# Revit family: Hager-GOLF-Flush_mounted-IP40-With_Cover-With_DIN-Hosted-CH-fr
name_source: partatom
category: Electrical Equipment
units: mm (PartAtom-declared; Revit-internal decimal feet)

## family parameters
Cut with Voids When Loaded = No
Host = Face
Maintain Annotation Orientation = Yes
Panel Configuration = Two Columns, Circuits Across
Part Type = Panelboard
Room Calculation Point = No
Round Connector Dimension = Use Diameter
Shared = No

## types (20) — shared parameters
BC_MODEL_ID = 1539117
BC_OBJECT_ID = 512264
BC_OBJECT_VERSION = #40
Code hager = ADD-EC000214_EU
EF000003 - Mounting method = Flush-mounted
EF000007 - Colour = White
EF000024 - UV resistant = No
EF000049 - Depth = 97 mm  [stored 0.318241 ft]
EF000116 - RAL-number = 9010
EF000118 - With mounting plate = No
EF000218 - Built-in depth = 72 mm  [stored 0.23622 ft]
EF001062 - EMC-version = No
EF001088 - Extension possible = Yes
EF001134 - DIN-rail = Yes
EF004462 - Type of closure = Other
EF005474 - Degree of protection (IP) = IP40
EF006306 - With lock = No
EF009212 - Cover model = Closed
EF015941 - Signal passing door = Yes
ETIM class code = EC000214
ETIM class name = Small distribution board
HG000001-Number of columns = 1
HG000002-With door or cover = Yes
HG000003-Range = GOLF
HG000005-Thickness = 2 mm  [stored 0.00656168 ft]
HG000006-Flush mounted = Yes
HG000009-Double swing door = No
HG000010-Asymmetric doors = No
HG000011-Empty rows from bottom = No
HG000012-Door swing angle = 90.00°
HG000013-Door on the left = No
HG000014-Door on the right = Yes
HG000015-Clearance visibility = Yes
HG000016-Door 3D visibility = Yes
HG000017-Distance between poles = 18 mm  [stored 0.0590551 ft]
HG000060-RAL-number = 9010
HG000099-Onfly Template ID = 507532
Manufacturer = Hager
Name = GOLF-Flush_mounted-IP40-With_Cover-With_DIN-CH
Name BIM&CO = Electricity
Name hager = ADD_Enclosures_EC000214
Uniformat = Low Tension Service & Dist.
Uniformat code = D501001
zero-valued in all types: Default Elevation, EF001131 - Inner depth, HG000007-Number of empty columns, HG000008-Number of empty rows

## per-type parameters (varying)
| type | BC_METADATA | BC_VARIANT_ID | EF000008 - Width | EF000040 - Height | EF000266 - Number of rows | EF000332 - Built-in height | EF000846 - Built-in width | EF002950 - Width in number of modular spacings | EF006244 - Transparent cover/door | EF015776 - Earthing terminal block | EF015777 - Neutral terminal block | HG000004-Manufacturer reference | HGEF000266-Number of rows | HGEF002950-Width in number of modular spacings |
| GOLF-Flush_mounted_W204_H225_D97_4_Modular_Spacing-VF104PS | {"ObjectGuid":"d3b36538-3273-4197-a562-01bf94599a27","ModelGuid":"35c68a91-80b1-4e81-b496-b66524f3143e","VariantGuid":"7900b5fb-65a8-428c-881f-07103e9f7ffe","Revision":"#25","VariantName":"GOLF-Flush_mounted_W204_H225_D97_4_Modular_Spacing-VF104PS"} | 1169077 | 204 mm | 225 mm  [stored 0.738189 ft] | 1 | 189 mm  [stored 0.620079 ft] | 170 mm  [stored 0.557743 ft] | 4 | No | No | No | VF104PS | 1 | 4 |
| GOLF-Flush_mounted_W204_H225_D97_4_Modular_Spacing-VF104TS | {"ObjectGuid":"d3b36538-3273-4197-a562-01bf94599a27","ModelGuid":"35c68a91-80b1-4e81-b496-b66524f3143e","VariantGuid":"d0b361cd-5e5f-4586-98f2-c8f494179b52","Revision":"#25","VariantName":"GOLF-Flush_mounted_W204_H225_D97_4_Modular_Spacing-VF104TS"} | 1169078 | 204 mm | 225 mm  [stored 0.738189 ft] | 1 | 189 mm  [stored 0.620079 ft] | 170 mm  [stored 0.557743 ft] | 4 | Yes | No | No | VF104TS | 1 | 4 |
| GOLF-Flush_mounted_W275_H225_D97_8_Modular_Spacing-VF108PS | {"ObjectGuid":"d3b36538-3273-4197-a562-01bf94599a27","ModelGuid":"35c68a91-80b1-4e81-b496-b66524f3143e","VariantGuid":"570270ab-bc6c-4446-b563-185213bbcdad","Revision":"#25","VariantName":"GOLF-Flush_mounted_W275_H225_D97_8_Modular_Spacing-VF108PS"} | 1169079 | 275 mm | 225 mm  [stored 0.738189 ft] | 1 | 189 mm  [stored 0.620079 ft] | 242 mm  [stored 0.793963 ft] | 8 | No | No | No | VF108PS | 1 | 8 |
| GOLF-Flush_mounted_W275_H225_D97_8_Modular_Spacing-VF108TS | {"ObjectGuid":"d3b36538-3273-4197-a562-01bf94599a27","ModelGuid":"35c68a91-80b1-4e81-b496-b66524f3143e","VariantGuid":"a5ca7ae0-c990-4f4f-958b-64a5adfce291","Revision":"#25","VariantName":"GOLF-Flush_mounted_W275_H225_D97_8_Modular_Spacing-VF108TS"} | 1169080 | 275 mm | 225 mm  [stored 0.738189 ft] | 1 | 189 mm  [stored 0.620079 ft] | 242 mm  [stored 0.793963 ft] | 8 | Yes | No | No | VF108TS | 1 | 8 |
| GOLF-Flush_mounted_W352_H293_D97_12_Modular_Spacing-VF112PS | {"ObjectGuid":"d3b36538-3273-4197-a562-01bf94599a27","ModelGuid":"35c68a91-80b1-4e81-b496-b66524f3143e","VariantGuid":"727fad79-9f42-4d6a-8770-c75fea08dc77","Revision":"#25","VariantName":"GOLF-Flush_mounted_W352_H293_D97_12_Modular_Spacing-VF112PS"} | 1169081 | 352 mm  [stored 1.15486 ft] | 293 mm | 1 | 257 mm  [stored 0.843176 ft] | 318 mm  [stored 1.04331 ft] | 12 | No | Yes | Yes | VF112PS | 1 | 12 |
| GOLF-Flush_mounted_W352_H293_D97_12_Modular_Spacing-VF112TS | {"ObjectGuid":"d3b36538-3273-4197-a562-01bf94599a27","ModelGuid":"35c68a91-80b1-4e81-b496-b66524f3143e","VariantGuid":"401b5175-9fe8-49df-9ccf-2e24f019ef7c","Revision":"#25","VariantName":"GOLF-Flush_mounted_W352_H293_D97_12_Modular_Spacing-VF112TS"} | 1169082 | 352 mm  [stored 1.15486 ft] | 293 mm | 1 | 257 mm  [stored 0.843176 ft] | 318 mm  [stored 1.04331 ft] | 12 | Yes | Yes | Yes | VF112TS | 1 | 12 |
| GOLF-Flush_mounted_W460_H293_D97_18_Modular_Spacing-VF118PS | {"ObjectGuid":"d3b36538-3273-4197-a562-01bf94599a27","ModelGuid":"35c68a91-80b1-4e81-b496-b66524f3143e","VariantGuid":"17cf55a8-2466-4161-94ee-1b10718c4a4d","Revision":"#25","VariantName":"GOLF-Flush_mounted_W460_H293_D97_18_Modular_Spacing-VF118PS"} | 1169083 | 460 mm  [stored 1.50919 ft] | 293 mm | 1 | 257 mm  [stored 0.843176 ft] | 426 mm  [stored 1.39764 ft] | 18 | No | Yes | Yes | VF118PS | 1 | 18 |
| GOLF-Flush_mounted_W460_H293_D97_18_Modular_Spacing-VF118TS | {"ObjectGuid":"d3b36538-3273-4197-a562-01bf94599a27","ModelGuid":"35c68a91-80b1-4e81-b496-b66524f3143e","VariantGuid":"f1381982-cb5e-465f-aaa6-3617943f5a5b","Revision":"#25","VariantName":"GOLF-Flush_mounted_W460_H293_D97_18_Modular_Spacing-VF118TS"} | 1169084 | 460 mm  [stored 1.50919 ft] | 293 mm | 1 | 257 mm  [stored 0.843176 ft] | 426 mm  [stored 1.39764 ft] | 18 | Yes | Yes | Yes | VF118TS | 1 | 18 |
| GOLF-Flush_mounted_W532_H293_D97_22_Modular_Spacing-VF122PS | {"ObjectGuid":"d3b36538-3273-4197-a562-01bf94599a27","ModelGuid":"35c68a91-80b1-4e81-b496-b66524f3143e","VariantGuid":"c0cb78b3-62a0-4b84-8207-cc9b2857fa89","Revision":"#25","VariantName":"GOLF-Flush_mounted_W532_H293_D97_22_Modular_Spacing-VF122PS"} | 1169085 | 532 mm  [stored 1.74541 ft] | 293 mm | 1 | 257 mm  [stored 0.843176 ft] | 498 mm  [stored 1.63386 ft] | 22 | No | Yes | Yes | VF122PS | 1 | 22 |
| GOLF-Flush_mounted_W532_H293_D97_22_Modular_Spacing-VF122TS | {"ObjectGuid":"d3b36538-3273-4197-a562-01bf94599a27","ModelGuid":"35c68a91-80b1-4e81-b496-b66524f3143e","VariantGuid":"293e72b4-7d50-44bc-9811-b4883de919bd","Revision":"#25","VariantName":"GOLF-Flush_mounted_W532_H293_D97_22_Modular_Spacing-VF122TS"} | 1169086 | 532 mm  [stored 1.74541 ft] | 293 mm | 1 | 257 mm  [stored 0.843176 ft] | 498 mm  [stored 1.63386 ft] | 22 | Yes | Yes | Yes | VF122TS | 1 | 22 |
| GOLF-Flush_mounted_W382_H418_D97_12_Modular_Spacing-VF212PS | {"ObjectGuid":"d3b36538-3273-4197-a562-01bf94599a27","ModelGuid":"35c68a91-80b1-4e81-b496-b66524f3143e","VariantGuid":"1c1d9eb9-c584-4ae0-8d83-5a1a4a7ae2db","Revision":"#25","VariantName":"GOLF-Flush_mounted_W382_H418_D97_12_Modular_Spacing-VF212PS"} | 1169087 | 382 mm  [stored 1.25328 ft] | 418 mm  [stored 1.37139 ft] | 2 | 382 mm  [stored 1.25328 ft] | 318 mm  [stored 1.04331 ft] | 12 | No | Yes | Yes | VF212PS | 2 | 12 |
| GOLF-Flush_mounted_W382_H418_D97_12_Modular_Spacing-VF212TS | {"ObjectGuid":"d3b36538-3273-4197-a562-01bf94599a27","ModelGuid":"35c68a91-80b1-4e81-b496-b66524f3143e","VariantGuid":"b39c769c-76a6-433b-92f8-836be028bd5e","Revision":"#25","VariantName":"GOLF-Flush_mounted_W382_H418_D97_12_Modular_Spacing-VF212TS"} | 1169088 | 382 mm  [stored 1.25328 ft] | 418 mm  [stored 1.37139 ft] | 2 | 382 mm  [stored 1.25328 ft] | 318 mm  [stored 1.04331 ft] | 12 | Yes | Yes | Yes | VF212TS | 2 | 12 |
| GOLF-Flush_mounted_W460_H418_D97_18_Modular_Spacing-VF218PS | {"ObjectGuid":"d3b36538-3273-4197-a562-01bf94599a27","ModelGuid":"35c68a91-80b1-4e81-b496-b66524f3143e","VariantGuid":"c172c064-34f9-4b63-bcd4-669eb244d423","Revision":"#25","VariantName":"GOLF-Flush_mounted_W460_H418_D97_18_Modular_Spacing-VF218PS"} | 1169089 | 460 mm  [stored 1.50919 ft] | 418 mm  [stored 1.37139 ft] | 2 | 382 mm  [stored 1.25328 ft] | 426 mm  [stored 1.39764 ft] | 18 | No | Yes | Yes | VF218PS | 2 | 18 |
| GOLF-Flush_mounted_W460_H418_D97_18_Modular_Spacing-VF218TS | {"ObjectGuid":"d3b36538-3273-4197-a562-01bf94599a27","ModelGuid":"35c68a91-80b1-4e81-b496-b66524f3143e","VariantGuid":"49bc955d-51bb-46dd-88d1-44fea68c0c1f","Revision":"#25","VariantName":"GOLF-Flush_mounted_W460_H418_D97_18_Modular_Spacing-VF218TS"} | 1169090 | 460 mm  [stored 1.50919 ft] | 418 mm  [stored 1.37139 ft] | 2 | 382 mm  [stored 1.25328 ft] | 426 mm  [stored 1.39764 ft] | 18 | Yes | Yes | Yes | VF218TS | 2 | 18 |
| GOLF-Flush_mounted_W352_H543_D97_12_Modular_Spacing-VF312PS | {"ObjectGuid":"d3b36538-3273-4197-a562-01bf94599a27","ModelGuid":"35c68a91-80b1-4e81-b496-b66524f3143e","VariantGuid":"c3d42502-f03b-433e-aa45-f362adffbda1","Revision":"#25","VariantName":"GOLF-Flush_mounted_W352_H543_D97_12_Modular_Spacing-VF312PS"} | 1169091 | 352 mm  [stored 1.15486 ft] | 543 mm  [stored 1.7815 ft] | 3 | 507 mm  [stored 1.66339 ft] | 318 mm  [stored 1.04331 ft] | 12 | No | Yes | Yes | VF312PS | 3 | 12 |
| GOLF-Flush_mounted_W352_H543_D97_12_Modular_Spacing-VF312TS | {"ObjectGuid":"d3b36538-3273-4197-a562-01bf94599a27","ModelGuid":"35c68a91-80b1-4e81-b496-b66524f3143e","VariantGuid":"f244ddc7-7657-477c-902d-df50d8065ce0","Revision":"#25","VariantName":"GOLF-Flush_mounted_W352_H543_D97_12_Modular_Spacing-VF312TS"} | 1169092 | 352 mm  [stored 1.15486 ft] | 543 mm  [stored 1.7815 ft] | 3 | 507 mm  [stored 1.66339 ft] | 318 mm  [stored 1.04331 ft] | 12 | Yes | Yes | Yes | VF312TS | 3 | 12 |
| GOLF-Flush_mounted_W460_H543_D97_18_Modular_Spacing-VF318PS | {"ObjectGuid":"d3b36538-3273-4197-a562-01bf94599a27","ModelGuid":"35c68a91-80b1-4e81-b496-b66524f3143e","VariantGuid":"c54b9e4d-c32e-4291-85e6-d57d915798a3","Revision":"#25","VariantName":"GOLF-Flush_mounted_W460_H543_D97_18_Modular_Spacing-VF318PS"} | 1169093 | 460 mm  [stored 1.50919 ft] | 543 mm  [stored 1.7815 ft] | 3 | 507 mm  [stored 1.66339 ft] | 426 mm  [stored 1.39764 ft] | 18 | No | Yes | Yes | VF318PS | 3 | 18 |
| GOLF-Flush_mounted_W460_H543_D97_18_Modular_Spacing-VF318TS | {"ObjectGuid":"d3b36538-3273-4197-a562-01bf94599a27","ModelGuid":"35c68a91-80b1-4e81-b496-b66524f3143e","VariantGuid":"40748570-5609-4b70-acc0-c072c51e99ec","Revision":"#25","VariantName":"GOLF-Flush_mounted_W460_H543_D97_18_Modular_Spacing-VF318TS"} | 1169094 | 460 mm  [stored 1.50919 ft] | 543 mm  [stored 1.7815 ft] | 3 | 507 mm  [stored 1.66339 ft] | 426 mm  [stored 1.39764 ft] | 18 | Yes | Yes | Yes | VF318TS | 3 | 18 |
| GOLF-Flush_mounted_W352_H688_D97_12_Modular_Spacing-VF412PS | {"ObjectGuid":"d3b36538-3273-4197-a562-01bf94599a27","ModelGuid":"35c68a91-80b1-4e81-b496-b66524f3143e","VariantGuid":"b52c81ad-5181-4532-9eef-0566acd4b8b8","Revision":"#25","VariantName":"GOLF-Flush_mounted_W352_H688_D97_12_Modular_Spacing-VF412PS"} | 1169095 | 352 mm  [stored 1.15486 ft] | 688 mm  [stored 2.25722 ft] | 4 | 652 mm  [stored 2.13911 ft] | 318 mm  [stored 1.04331 ft] | 12 | No | Yes | Yes | VF412PS | 4 | 12 |
| GOLF-Flush_mounted_W460_H688_D97_18_Modular_Spacing-VF418PS | {"ObjectGuid":"d3b36538-3273-4197-a562-01bf94599a27","ModelGuid":"35c68a91-80b1-4e81-b496-b66524f3143e","VariantGuid":"9c3bfeb1-8f96-4eba-b4b7-d07036a65564","Revision":"#25","VariantName":"GOLF-Flush_mounted_W460_H688_D97_18_Modular_Spacing-VF418PS"} | 1169096 | 460 mm  [stored 1.50919 ft] | 688 mm  [stored 2.25722 ft] | 4 | 652 mm  [stored 2.13911 ft] | 426 mm  [stored 1.39764 ft] | 18 | No | Yes | Yes | VF418PS | 4 | 18 |

note: column(s) folded — value = type name in every type: Reference

note: [stored X ft] marks values corroborated as IEEE doubles in the binary element streams (Revit-internal decimal feet)

## geometry (parser evidence)
native form markers: Sweep x13
no freeform markers — native parametric forms only
